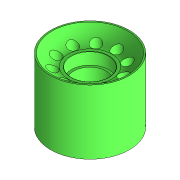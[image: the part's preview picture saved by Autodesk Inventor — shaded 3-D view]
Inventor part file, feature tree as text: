
AUTODESK INVENTOR PART (.ipt)
format: ipt  version: 2017 (Build 210142000, 142)  size: 305,152 bytes
history: native  units: mm
features: sketch x5, extrude x4, mirror x2, fillet x2, revolve x1, pattern_circular x1, plane x1
ambient origin geometry x8: Origin, YZ Plane, XZ Plane, XY Plane, X Axis, Y Axis, Z Axis, Center Point
bodies: Solid1 (feature_tree)
feature tree (16):
  extrude  "Extrusion1"  Depth=19.0mm
  extrude  "Extrusion2"  Depth=31.7mm
  revolve  "Revolution1"  [1 undecoded]
  mirror  "Mirror2"
  fillet  "Fillet1"  Radius=100.0mm
  extrude  "Extrusion4"  Depth=30.0mm
  pattern_circular  "Circular Pattern1"  [2 undecoded]
  plane  "Work Plane1"
  extrude  "Extrusion5"  Depth=0.2mm
  mirror  "Mirror3"
  fillet  "Fillet5"  Radius=12.0mm
  sketch  "Sketch1"  dims[d0=38.0mm d1=0.0mm d2=19.0mm]
  sketch  "Sketch2"  dims[d3=56.0mm d4=0.0mm d8=31.7mm]
  sketch  "Sketch4"  dims[d9=5.8mm d10=60.75mm d11=0.0mm d12=100.0mm d13=360.0deg]
  sketch  "Sketch5"  dims[d15=46.6mm d18=30.0mm]
  sketch  "Sketch7"  dims[d19=90.0deg d20=10.0mm d31=44.8mm d32=12.0mm d33=5.0mm d34=22.0mm d35=20.0mm d36=0.0mm d37=0.2mm]
note: 3 required parameter values undecoded (feature->parameter linkage not recoverable at this tier; creation-order binding heuristic only, values carry confidence <= 0.55)